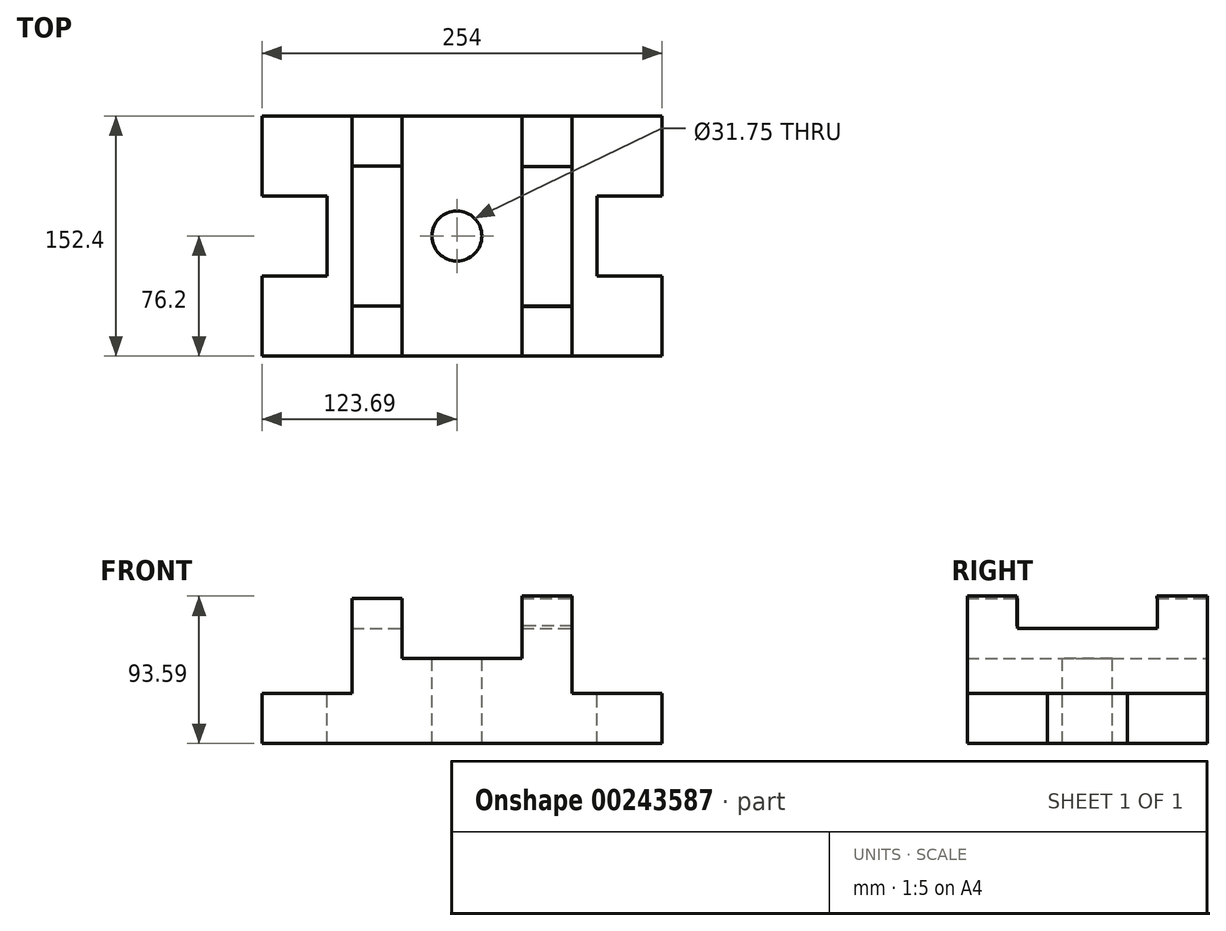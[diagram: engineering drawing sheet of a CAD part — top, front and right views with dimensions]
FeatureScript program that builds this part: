
annotation { "Feature Type Name" : "Feature", "Feature Type Description" : "" }
export const myFeature = defineFeature(function(context is Context, id is Id, definition is map)
    precondition{}
    {
        {
            var Q0;
            Q0=qCreatedBy(makeId("Front.planeOp"),FACE);
            var sketch = newSketch(context, id + "F0", { "sketchPlane" : qUnion([Q0])});
            skLineSegment(sketch, "E0.bottom", {"start": v(-127.45, -6.52) * mm, "end": v(126.55, -6.52) * mm});
            skLineSegment(sketch, "E0.top", {"start": v(-127.45, -38.27) * mm, "end": v(126.55, -38.27) * mm});
            skLineSegment(sketch, "E0.left", {"start": v(-127.45, -6.52) * mm, "end": v(-127.45, -38.27) * mm});
            skLineSegment(sketch, "E0.right", {"start": v(126.55, -6.52) * mm, "end": v(126.55, -38.27) * mm});
            skLineSegment(sketch, "E1.top", {"start": v(-70.3, 53.8) * mm, "end": v(-38.55, 53.8) * mm});
            skLineSegment(sketch, "E1.left", {"start": v(-70.3, -6.52) * mm, "end": v(-70.3, 53.8) * mm});
            skLineSegment(sketch, "E1.right", {"start": v(-38.55, -6.52) * mm, "end": v(-38.55, 53.8) * mm});
            skLineSegment(sketch, "E2.top", {"start": v(69.4, 55.32) * mm, "end": v(37.65, 55.32) * mm});
            skLineSegment(sketch, "E2.left", {"start": v(69.4, -6.52) * mm, "end": v(69.4, 55.32) * mm});
            skLineSegment(sketch, "E2.right", {"start": v(37.65, -6.52) * mm, "end": v(37.65, 55.32) * mm});
            skLineSegment(sketch, "E3.top", {"start": v(-38.55, 15.7) * mm, "end": v(37.65, 15.7) * mm});
            skLineSegment(sketch, "E3.left", {"start": v(-38.55, -6.52) * mm, "end": v(-38.55, 15.7) * mm});
            skLineSegment(sketch, "E3.right", {"start": v(37.65, -6.52) * mm, "end": v(37.65, 15.7) * mm});
            skSolve(sketch);
        }
        {
            var Q0;
            Q0 = qSketchRegion(id + "F0", true);
            extrude(context, id + "F1", {"entities" : qUnion([Q0]), "depth" : 152.4 * mm});
        }
        {
            var Q0;
            Q0=makeQuery(id+"F1.opExtrude","SWEPT_FACE",FACE,{"disambiguationData":[OSD([sQuery(id+"F0.wireOp",EDGE,"E1.top")])]});
            var sketch = newSketch(context, id + "F2", { "sketchPlane" : qUnion([Q0])});
            skLineSegment(sketch, "E4.bottom", {"start": v(-70.3, -31.75) * mm, "end": v(-38.55, -31.75) * mm});
            skLineSegment(sketch, "E4.top", {"start": v(-70.3, -120.65) * mm, "end": v(-38.55, -120.65) * mm});
            skLineSegment(sketch, "E4.left", {"start": v(-70.3, -31.75) * mm, "end": v(-70.3, -120.65) * mm});
            skLineSegment(sketch, "E4.right", {"start": v(-38.55, -31.75) * mm, "end": v(-38.55, -120.65) * mm});
            skLineSegment(sketch, "E5.bottom", {"start": v(37.65, -120.65) * mm, "end": v(69.4, -120.65) * mm});
            skLineSegment(sketch, "E5.top", {"start": v(37.65, -31.75) * mm, "end": v(69.4, -31.75) * mm});
            skLineSegment(sketch, "E5.right", {"start": v(69.4, -120.65) * mm, "end": v(69.4, -31.75) * mm});
            skLineSegment(sketch, "E6", {"start": v(37.65, -31.75) * mm, "end": v(37.65, -120.65) * mm});
            skSolve(sketch);
        }
        {
            var Q0;
            Q0 = qSketchRegion(id + "F2", true);
            extrude(context, id + "F3", {"entities" : qUnion([Q0]), "operationType" : NewBodyOperationType.REMOVE, "oppositeDirection" : true, "depth" : 19.05 * mm});
        }
        {
            var Q0;
            Q0=makeQuery(id+"F1.opExtrude","SWEPT_FACE",FACE,{"disambiguationData":[OSD([sQuery(id+"F0.wireOp",EDGE,"E2.top")])]});
            var sketch = newSketch(context, id + "F4", { "sketchPlane" : qUnion([Q0])});
            skLineSegment(sketch, "E7.bottom", {"start": v(37.65, -32.12) * mm, "end": v(69.4, -32.12) * mm});
            skLineSegment(sketch, "E7.top", {"start": v(37.65, -121.02) * mm, "end": v(69.4, -121.02) * mm});
            skLineSegment(sketch, "E7.left", {"start": v(37.65, -32.12) * mm, "end": v(37.65, -121.02) * mm});
            skLineSegment(sketch, "E7.right", {"start": v(69.4, -32.12) * mm, "end": v(69.4, -121.02) * mm});
            skSolve(sketch);
        }
        {
            var Q0;
            Q0=makeQuery(id+"F4.imprint","IMPRINT",FACE,{"disambiguationData":[TD([[makeQuery(id+"F4.imprint","IMPRINT",EDGE,{"derivedFrom":sQuery(id+"F4.wireOp",EDGE,"E7.bottom")}),-1.0]])]});
            extrude(context, id + "F5", {"entities" : qUnion([Q0]), "operationType" : NewBodyOperationType.REMOVE, "oppositeDirection" : true, "depth" : 19.05 * mm});
        }
        {
            var Q0;
            Q0=makeQuery(id+"F1.opExtrude","SWEPT_FACE",FACE,{"disambiguationData":[OSD([sQuery(id+"F0.wireOp",EDGE,"E3.top")])]});
            var sketch = newSketch(context, id + "F6", { "sketchPlane" : qUnion([Q0])});
            skCircle(sketch, "E8", {"center": v(-3.76, -76.2) * mm, "radius": 15.88 * mm});
            skSolve(sketch);
        }
        {
            var Q0;
            Q0=makeQuery(id+"F6.imprint","IMPRINT",FACE,{"disambiguationData":[TD([[makeQuery(id+"F6.imprint","IMPRINT",EDGE,{"derivedFrom":sQuery(id+"F6.wireOp",EDGE,"E8")}),1.0]])]});
            extrude(context, id + "F7", {"entities" : qUnion([Q0]), "operationType" : NewBodyOperationType.REMOVE, "oppositeDirection" : true, "depth" : 53.97 * mm});
        }
        {
            var Q0;
            {var subQ0=sQuery(id+"F0.wireOp",EDGE,"E0.bottom");Q0=makeQuery(id+"F1.opExtrude","SWEPT_FACE",FACE,{"disambiguationData":[OSD([subQ0]),TDD([makeQuery(id+"F0.imprint","IMPRINT",EDGE,{"disambiguationData":[TD([[makeQuery(id+"F0.imprint","INTERSECT",VERTEX,{"derivedFrom":[subQ0,sQuery(id+"F0.wireOp",EDGE,"E0.left")]}),-1.0]])],"derivedFrom":subQ0})])]});}
            var sketch = newSketch(context, id + "F8", { "sketchPlane" : qUnion([Q0])});
            skLineSegment(sketch, "E9.bottom", {"start": v(-127.45, -50.8) * mm, "end": v(-86.18, -50.8) * mm});
            skLineSegment(sketch, "E9.top", {"start": v(-127.45, -101.6) * mm, "end": v(-86.18, -101.6) * mm});
            skLineSegment(sketch, "E9.left", {"start": v(-127.45, -50.8) * mm, "end": v(-127.45, -101.6) * mm});
            skLineSegment(sketch, "E9.right", {"start": v(-86.18, -50.8) * mm, "end": v(-86.18, -101.6) * mm});
            skSolve(sketch);
        }
        {
            var Q0;
            Q0 = qSketchRegion(id + "F8", true);
            extrude(context, id + "F9", {"entities" : qUnion([Q0]), "operationType" : NewBodyOperationType.REMOVE, "oppositeDirection" : true, "depth" : 31.75 * mm});
        }
        {
            var Q0;
            {var subQ0=sQuery(id+"F0.wireOp",EDGE,"E0.bottom");Q0=makeQuery(id+"F1.opExtrude","SWEPT_FACE",FACE,{"disambiguationData":[OSD([subQ0]),TDD([makeQuery(id+"F0.imprint","IMPRINT",EDGE,{"disambiguationData":[TD([[makeQuery(id+"F0.imprint","INTERSECT",VERTEX,{"derivedFrom":[subQ0,sQuery(id+"F0.wireOp",EDGE,"E0.right")]}),1.0]])],"derivedFrom":subQ0})])]});}
            var sketch = newSketch(context, id + "F10", { "sketchPlane" : qUnion([Q0])});
            skLineSegment(sketch, "E10.bottom", {"start": v(126.55, -50.8) * mm, "end": v(85.27, -50.8) * mm});
            skLineSegment(sketch, "E10.top", {"start": v(126.55, -101.6) * mm, "end": v(85.27, -101.6) * mm});
            skLineSegment(sketch, "E10.left", {"start": v(126.55, -50.8) * mm, "end": v(126.55, -101.6) * mm});
            skLineSegment(sketch, "E10.right", {"start": v(85.27, -50.8) * mm, "end": v(85.27, -101.6) * mm});
            skSolve(sketch);
        }
        {
            var Q0;
            Q0 = qSketchRegion(id + "F10", true);
            extrude(context, id + "F11", {"entities" : qUnion([Q0]), "operationType" : NewBodyOperationType.REMOVE, "oppositeDirection" : true, "depth" : 31.75 * mm});
        }
    });
